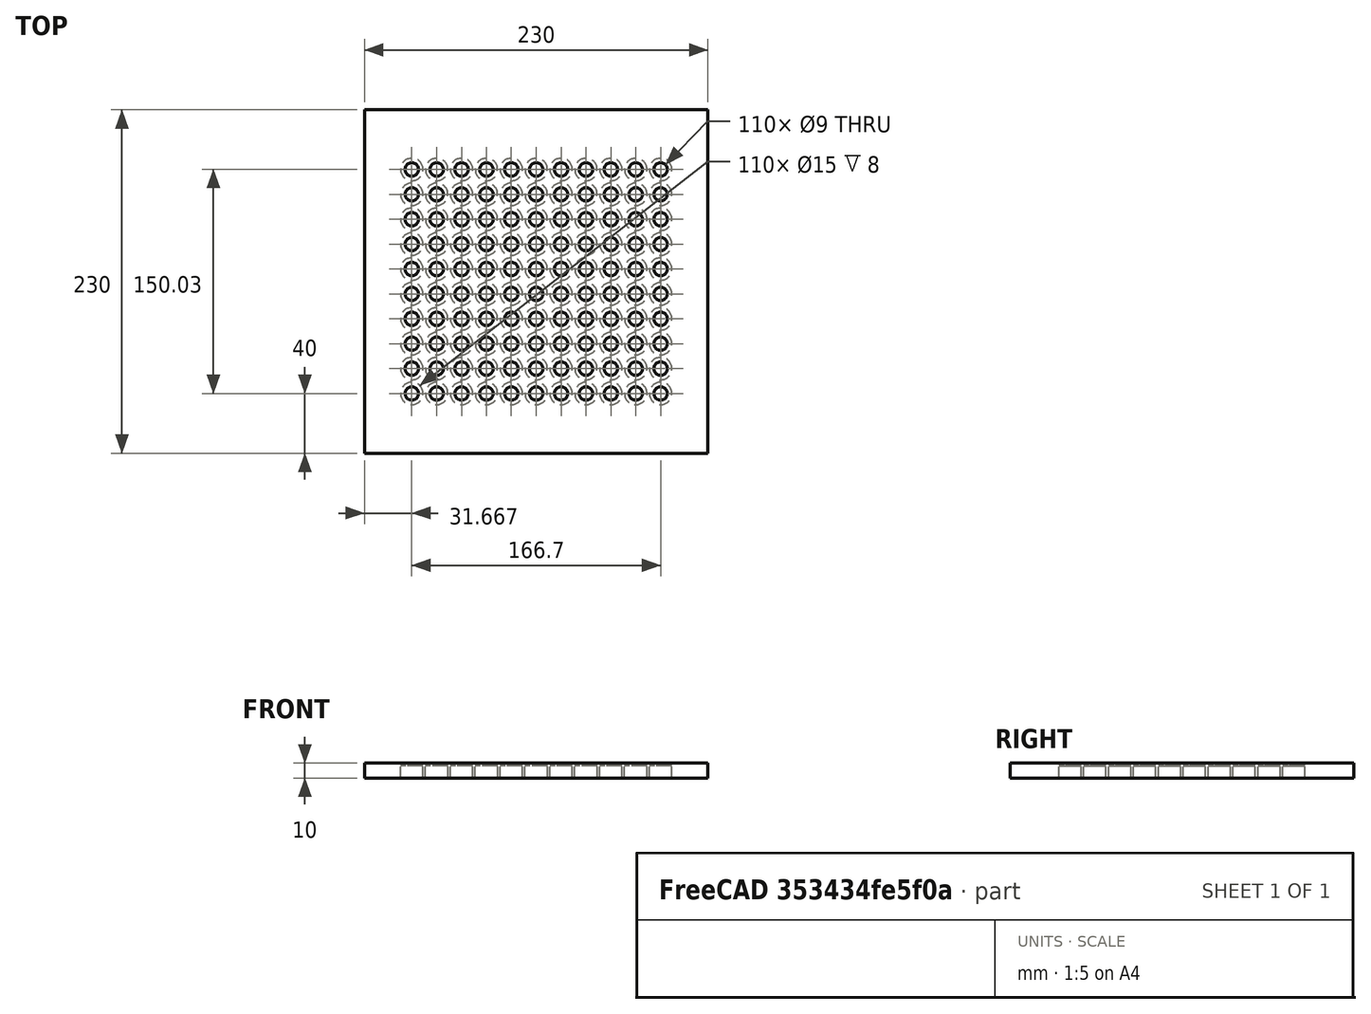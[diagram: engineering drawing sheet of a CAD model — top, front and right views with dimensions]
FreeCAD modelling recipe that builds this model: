
FCSTD DOCUMENT  (FreeCAD 0.14R3702 (Git))
Label: LED-Matrix
License: CC-BY 3.0
LicenseURL: http://creativecommons.org/licenses/by/3.0/
objects: Part::Cylinder×2, Part::Cut×2, Part::Box×1, Part::MultiFuse×1, Part::FeaturePython×1
note: 7 computed .brp shape members not serialized (recipe doc carries the construction recipe); baked Part::Feature solids carry a one-line shape summary decoded from their .brp

FEATURE [Part::Box] Box  label="Cube"
  Height = 10
  Length = 230
  Width = 230
FEATURE [Part::Cylinder] Cylinder  label="Zylinder"
  Angle = 360
  Height = 8
  Placement = pos=(31.6667,40,0) rot=(0,0,1;0rad)
  Radius = 7.5
FEATURE [Part::Cylinder] Cylinder001  label="Zylinder001"
  Angle = 360
  Height = 10
  Placement = pos=(31.6667,40,0) rot=(0,0,1;0rad)
  Radius = 4.5
FEATURE [Part::MultiFuse] Fusion
  Shapes = -> [Cylinder,Cylinder001]
FEATURE [Part::Cut] Cut
  Base = -> Box
  Tool = -> Fusion
FEATURE [Part::FeaturePython] Array  # Draft array (typed FeaturePython)
  Angle = 360
  ArrayType = 0
  Axis = (0,0,1)
  Base = -> Fusion
  Center = (0,0,0)
  IntervalX = (16.67,0,0)
  IntervalY = (0,16.67,0)
  IntervalZ = (0,0,1)
  NumberPolar = 1
  NumberX = 11
  NumberY = 10
  NumberZ = 1
FEATURE [Part::Cut] Cut001
  Base = -> Cut
  Tool = -> Array
